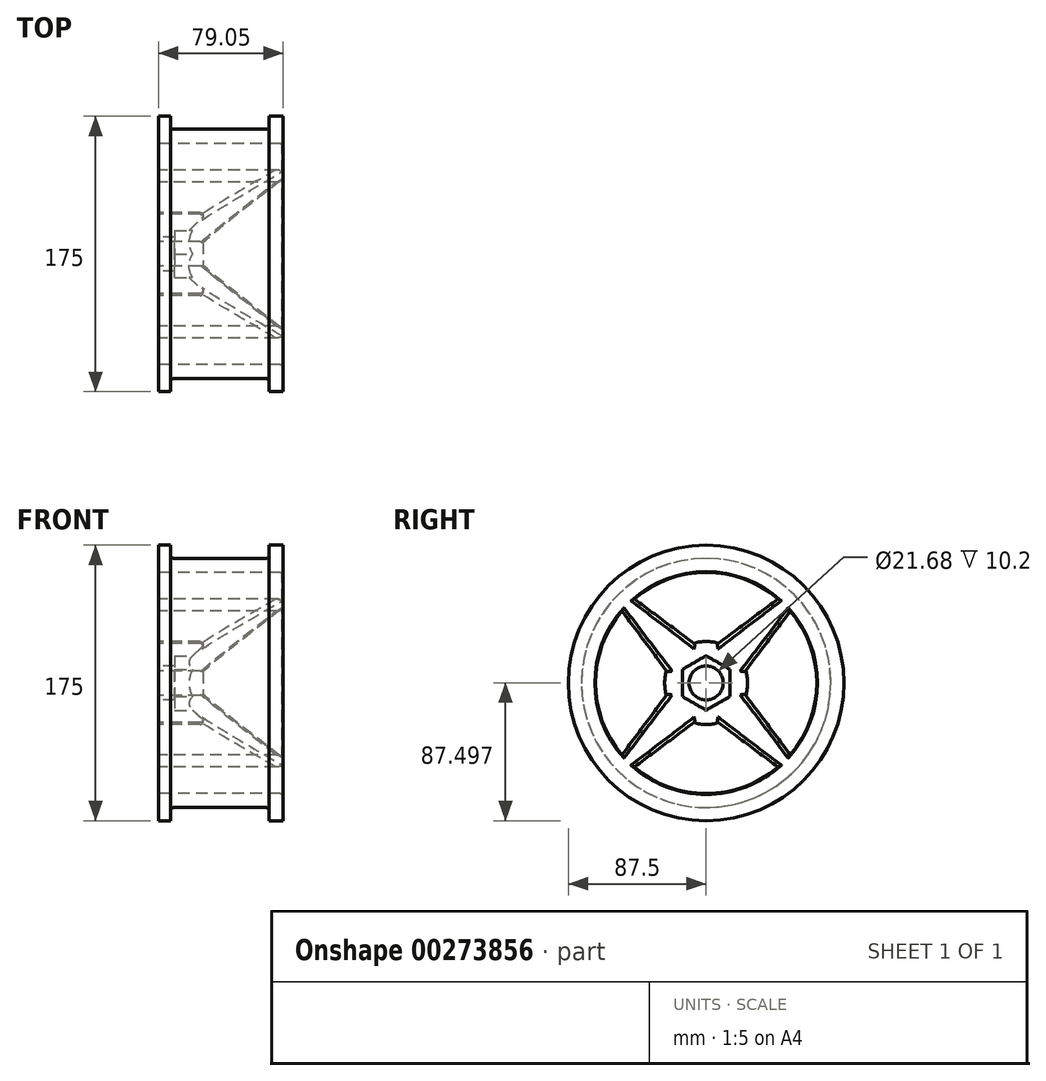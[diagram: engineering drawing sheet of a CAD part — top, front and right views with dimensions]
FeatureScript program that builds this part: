
annotation { "Feature Type Name" : "Feature", "Feature Type Description" : "" }
export const myFeature = defineFeature(function(context is Context, id is Id, definition is map)
    precondition{}
    {
        {
            var Q0;
            Q0=qCreatedBy(makeId("Front.planeOp"),FACE);
            var sketch = newSketch(context, id + "F0", { "sketchPlane" : qUnion([Q0])});
            skLineSegment(sketch, "E0", {"start": v(-67.1, -42.56) * mm, "end": v(-67.1, 34.1) * mm});
            skLineSegment(sketch, "E1", {"start": v(-67.1, 34.1) * mm, "end": v(-59.48, 34.1) * mm});
            skLineSegment(sketch, "E2", {"start": v(11.95, 34.1) * mm, "end": v(11.95, 17.85) * mm});
            skLineSegment(sketch, "E3", {"start": v(11.95, 17.85) * mm, "end": v(-52.28, -42.56) * mm});
            skLineSegment(sketch, "E4", {"start": v(-52.28, -42.56) * mm, "end": v(-67.1, -42.56) * mm});
            skLineSegment(sketch, "E5", {"start": v(-69.8, -53.4) * mm, "end": v(-40.16, -53.4) * mm});
            skLineSegment(sketch, "E6", {"start": v(-59.48, 34.1) * mm, "end": v(-59.48, 25.78) * mm});
            skLineSegment(sketch, "E7", {"start": v(-59.48, 25.78) * mm, "end": v(3.18, 25.78) * mm});
            skLineSegment(sketch, "E8", {"start": v(3.18, 25.78) * mm, "end": v(3.18, 34.1) * mm});
            skLineSegment(sketch, "E9.trimOffspring", {"start": v(3.18, 34.1) * mm, "end": v(11.95, 34.1) * mm});
            skSolve(sketch);
        }
        {
            var Q0;
            Q0 = qSketchRegion(id + "F0", true);
            var Q1;
            Q1=sQuery(id+"F0.wireOp",EDGE,"E5");
            revolve(context, id + "F1", {"entities" : qUnion([Q0]), "axis" : qUnion([Q1]), "revolveType" : RevolveType.FULL});
        }
        {
            var Q0;
            Q0=makeQuery(id+"F1.opRevolve","SWEPT_FACE",FACE,{"disambiguationData":[OSD([sQuery(id+"F0.wireOp",EDGE,"E0")])]});
            var sketch = newSketch(context, id + "F2", { "sketchPlane" : qUnion([Q0])});
            skLineSegment(sketch, "E10", {"start": v(-7.8, -28.21) * mm, "end": v(-45.64, 0) * mm});
            skLineSegment(sketch, "E11", {"start": v(0, -53.4) * mm, "end": v(0, 23.28) * mm, "construction": true});
            skLineSegment(sketch, "E12.MirrorCS", {"start": v(7.8, -28.21) * mm, "end": v(45.64, 0) * mm});
            skArc(sketch, "E13", {"start": v(7.8, -28.21) * mm, "mid": v(0, -27.03) * mm, "end": v(-7.8, -28.21) * mm});
            skArc(sketch, "E14", {"start": v(45.64, 0) * mm, "mid": v(0, 16.85) * mm, "end": v(-45.64, 0) * mm});
            skPoint(sketch, "E15.orphan", {"position": v(-4.4, -30.74) * mm});
            skPoint(sketch, "E16.orphan", {"position": v(4.4, -30.74) * mm});
            skPoint(sketch, "E17.orphan", {"position": v(42.65, -2.22) * mm});
            skPoint(sketch, "E18.orphan", {"position": v(-42.65, -2.22) * mm});
            skPoint(sketch, "E19.1.0", {"position": v(-51.17, -10.74) * mm});
            skArc(sketch, "E19.1.1", {"start": v(-53.4, -7.76) * mm, "mid": v(-70.24, -53.4) * mm, "end": v(-53.4, -99.03) * mm});
            skPoint(sketch, "E19.1.2", {"position": v(-51.17, -96.05) * mm});
            skPoint(sketch, "E19.1.3", {"position": v(-22.65, -57.8) * mm});
            skLineSegment(sketch, "E19.1.4", {"start": v(-25.18, -61.2) * mm, "end": v(-53.4, -99.03) * mm});
            skPoint(sketch, "E19.1.5", {"position": v(-22.65, -48.99) * mm});
            skLineSegment(sketch, "E19.1.6", {"start": v(-25.18, -45.6) * mm, "end": v(-53.4, -7.76) * mm});
            skArc(sketch, "E19.1.7", {"start": v(-25.18, -45.6) * mm, "mid": v(-26.36, -53.4) * mm, "end": v(-25.18, -61.2) * mm});
            skPoint(sketch, "E19.2.0", {"position": v(-42.65, -104.56) * mm});
            skArc(sketch, "E19.2.1", {"start": v(-45.64, -106.79) * mm, "mid": v(0, -123.63) * mm, "end": v(45.64, -106.79) * mm});
            skPoint(sketch, "E19.2.2", {"position": v(42.65, -104.56) * mm});
            skPoint(sketch, "E19.2.3", {"position": v(4.4, -76.04) * mm});
            skLineSegment(sketch, "E19.2.4", {"start": v(7.8, -78.57) * mm, "end": v(45.64, -106.79) * mm});
            skPoint(sketch, "E19.2.5", {"position": v(-4.4, -76.04) * mm});
            skLineSegment(sketch, "E19.2.6", {"start": v(-7.8, -78.57) * mm, "end": v(-45.64, -106.79) * mm});
            skArc(sketch, "E19.2.7", {"start": v(-7.8, -78.57) * mm, "mid": v(0, -79.75) * mm, "end": v(7.8, -78.57) * mm});
            skArc(sketch, "E20.1.3.0", {"start": v(53.4, -99.03) * mm, "mid": v(70.24, -53.4) * mm, "end": v(53.4, -7.76) * mm});
            skPoint(sketch, "E20.2.3.0", {"position": v(51.17, -96.05) * mm});
            skPoint(sketch, "E20.5.3.0", {"position": v(51.17, -10.74) * mm});
            skPoint(sketch, "E20.6.3.0", {"position": v(22.65, -48.99) * mm});
            skLineSegment(sketch, "E20.7.3.0", {"start": v(25.18, -45.6) * mm, "end": v(53.4, -7.76) * mm});
            skPoint(sketch, "E20.10.3.0", {"position": v(22.65, -57.8) * mm});
            skLineSegment(sketch, "E20.11.3.0", {"start": v(25.18, -61.2) * mm, "end": v(53.4, -99.03) * mm});
            skArc(sketch, "E20.14.3.0", {"start": v(25.18, -61.2) * mm, "mid": v(26.36, -53.4) * mm, "end": v(25.18, -45.6) * mm});
            skSolve(sketch);
        }
        {
            var Q0;
            Q0 = qSketchRegion(id + "F2", true);
            extrude(context, id + "F3", {"entities" : qUnion([Q0]), "operationType" : NewBodyOperationType.REMOVE, "endBound" : BoundingType.THROUGH_ALL, "oppositeDirection" : true, "depth" : 25.4 * mm});
        }
        {
            var Q0;
            Q0=makeQuery(id+"F1.opRevolve","SWEPT_FACE",FACE,{"disambiguationData":[OSD([sQuery(id+"F0.wireOp",EDGE,"E3")])]});
            fillet(context, id + "F4", {"entities" : qUnion([Q0]), "radius" : 2 * mm, "tangentPropagation" : true, "allowEdgeOverflow" : false});
        }
        {
            var Q0;
            Q0=makeQuery(id+"F1.opRevolve","SWEPT_EDGE",EDGE,{"disambiguationData":[OSD([sQuery(id+"F0.wireOp",EDGE,"E7"),sQuery(id+"F0.wireOp",EDGE,"E8")])]});
            var Q1;
            Q1=makeQuery(id+"F1.opRevolve","SWEPT_EDGE",EDGE,{"disambiguationData":[OSD([sQuery(id+"F0.wireOp",EDGE,"E6"),sQuery(id+"F0.wireOp",EDGE,"E7")])]});
            fillet(context, id + "F5", {"entities" : qUnion([Q0, Q1]), "radius" : 2 * mm, "tangentPropagation" : true, "allowEdgeOverflow" : false});
        }
        {
            var Q0;
            Q0=qCreatedBy(makeId("Right.planeOp"),FACE);
            cPlane(context, id + "F6", {"entities" : qUnion([Q0]), "cplaneType" : CPlaneType.OFFSET, "offset" : 25 * mm, "oppositeDirection" : true, "width" : 150 * mm, "height" : 150 * mm});
        }
        {
            var Q0;
            Q0=qCreatedBy(id+"F6.planeOp",FACE);
            var sketch = newSketch(context, id + "F7", { "sketchPlane" : qUnion([Q0])});
            skCircle(sketch, "E21.cCircle", {"center": v(0, -53.4) * mm, "radius": 15 * mm, "construction": true});
            skLineSegment(sketch, "E21.0", {"start": v(15, -62.05) * mm, "end": v(0, -70.71) * mm});
            skLineSegment(sketch, "E21.1", {"start": v(0, -70.71) * mm, "end": v(-15, -62.05) * mm});
            skLineSegment(sketch, "E21.2", {"start": v(-15, -62.05) * mm, "end": v(-15, -44.73) * mm});
            skLineSegment(sketch, "E21.3", {"start": v(-15, -44.73) * mm, "end": v(0, -36.07) * mm});
            skLineSegment(sketch, "E21.4", {"start": v(0, -36.07) * mm, "end": v(15, -44.73) * mm});
            skLineSegment(sketch, "E21.5", {"start": v(15, -44.73) * mm, "end": v(15, -62.05) * mm});
            skPoint(sketch, "E21.0.midPoint", {"position": v(7.5, -66.38) * mm});
            skSolve(sketch);
        }
        {
            var Q0;
            Q0 = qSketchRegion(id + "F7", true);
            extrude(context, id + "F8", {"entities" : qUnion([Q0]), "operationType" : NewBodyOperationType.REMOVE, "oppositeDirection" : true, "depth" : 31.9 * mm});
        }
    });
